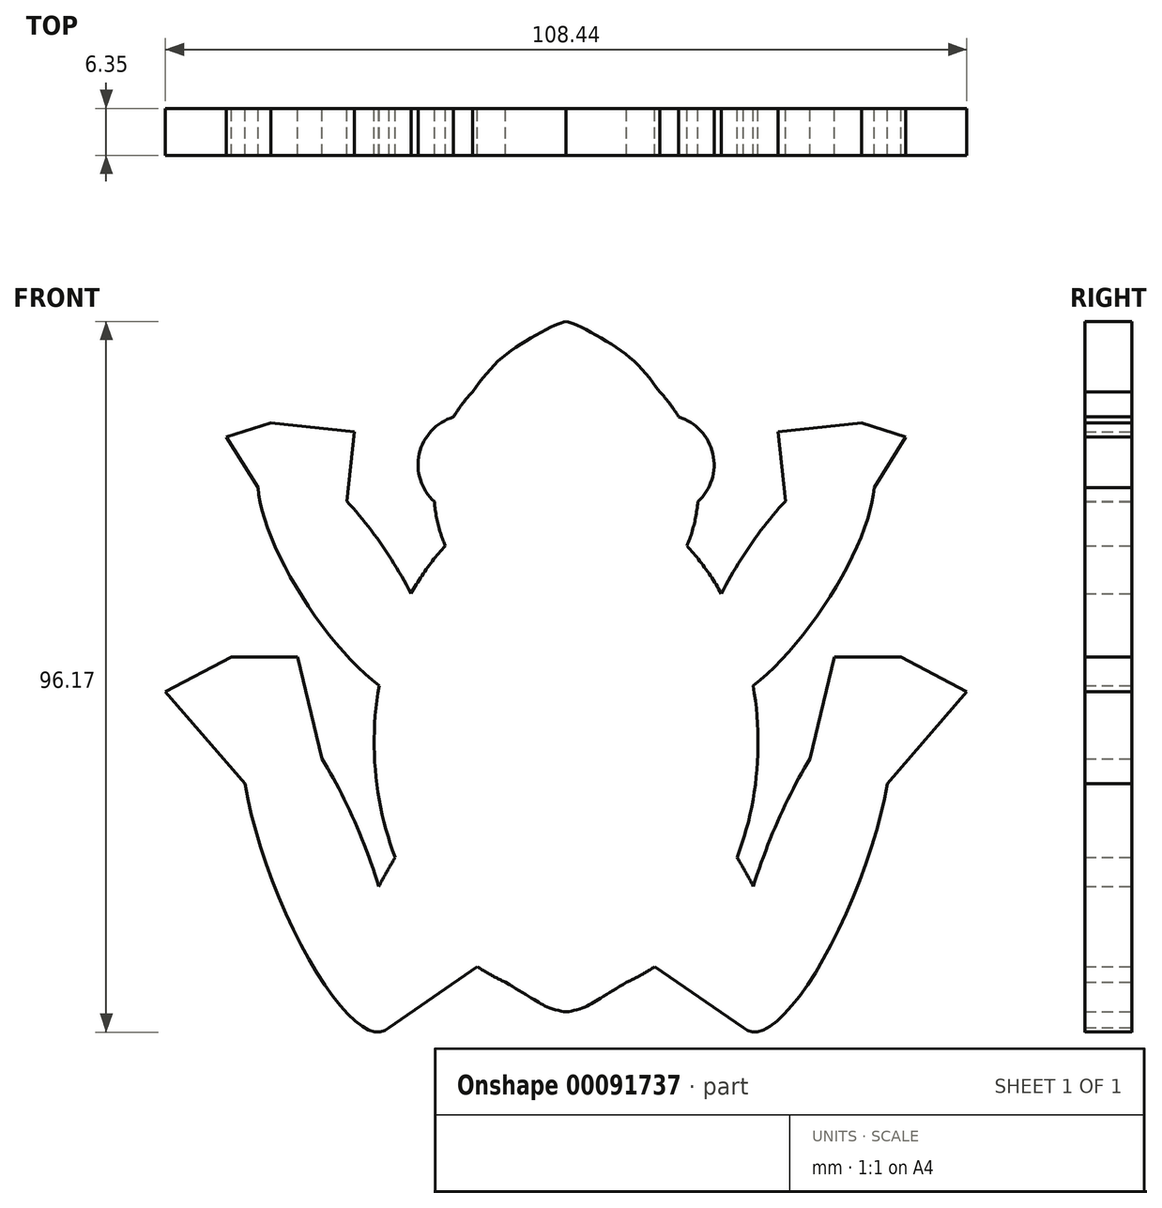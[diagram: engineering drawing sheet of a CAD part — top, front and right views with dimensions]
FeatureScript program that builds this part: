
annotation { "Feature Type Name" : "Feature", "Feature Type Description" : "" }
export const myFeature = defineFeature(function(context is Context, id is Id, definition is map)
    precondition{}
    {
        {
            var Q0;
            Q0=qCreatedBy(makeId("Front.planeOp"),FACE);
            var sketch = newSketch(context, id + "F0", { "sketchPlane" : qUnion([Q0])});
            skLineSegment(sketch, "E0", {"start": v(0, 61.38) * mm, "end": v(0, -64.6) * mm, "construction": true});
            skEllipticalArc(sketch, "E1", {});
            skEllipticalArc(sketch, "E2", {});
            skEllipticalArc(sketch, "E3", {});
            skEllipticalArc(sketch, "E4.trimOffspring", {});
            skEllipticalArc(sketch, "E5.trimOffspring", {});
            skEllipticalArc(sketch, "E6.trimOffspring", {});
            skEllipticalArc(sketch, "E7.trimOffspring", {});
            skArc(sketch, "E8", {"start": v(-15.23, 44.04) * mm, "mid": v(-19.86, 39.05) * mm, "end": v(-17.82, 32.57) * mm});
            skFitSpline(sketch, "E9", {"points": [v(-12.67, 47.44) * mm, v(-9.33, 51.47) * mm, v(-5.1, 54.5) * mm, v(-1.15, 56.62) * mm, v(0, 56.95) * mm], "startDerivative": vector(10.66, 14.6) * mm, "endDerivative": vector(7.04, 1.42) * mm});
            skEllipticalArc(sketch, "E10.trimOffspring", {});
            skFitSpline(sketch, "E11", {"points": [v(-8.18, -32.47) * mm, v(-4.1, -34.97) * mm, v(-2.03, -36) * mm, v(0, -36.45) * mm, v(0, -36.37) * mm], "startDerivative": vector(11.27, -6.95) * mm, "endDerivative": vector(-0.7, 1.73) * mm});
            skLineSegment(sketch, "E12", {"start": v(-41.7, 34.5) * mm, "end": v(-45.98, 41.36) * mm});
            skLineSegment(sketch, "E13", {"start": v(-45.98, 41.36) * mm, "end": v(-39.98, 43.24) * mm});
            skLineSegment(sketch, "E14", {"start": v(-39.98, 43.24) * mm, "end": v(-28.67, 42.02) * mm});
            skLineSegment(sketch, "E15", {"start": v(-28.67, 42.02) * mm, "end": v(-29.68, 32.66) * mm});
            skLineSegment(sketch, "E16", {"start": v(-43.48, -5.56) * mm, "end": v(-54.22, 6.86) * mm});
            skLineSegment(sketch, "E17", {"start": v(-54.22, 6.86) * mm, "end": v(-45.3, 11.53) * mm});
            skLineSegment(sketch, "E18", {"start": v(-45.3, 11.53) * mm, "end": v(-36.32, 11.53) * mm});
            skLineSegment(sketch, "E19", {"start": v(-36.32, 11.53) * mm, "end": v(-33, -2.25) * mm});
            skEllipticalArc(sketch, "E20.trimOffspring", {});
            skEllipticalArc(sketch, "E21.trimOffspring", {});
            skLineSegment(sketch, "E22.MirrorCS", {"start": v(45.98, 41.36) * mm, "end": v(39.98, 43.24) * mm});
            skLineSegment(sketch, "E23.MirrorCS", {"start": v(39.98, 43.24) * mm, "end": v(28.67, 42.02) * mm});
            skLineSegment(sketch, "E24.MirrorCS", {"start": v(28.67, 42.02) * mm, "end": v(29.68, 32.66) * mm});
            skLineSegment(sketch, "E25.MirrorCS", {"start": v(41.7, 34.5) * mm, "end": v(45.98, 41.36) * mm});
            skEllipticalArc(sketch, "E26.MirrorCS", {});
            skEllipticalArc(sketch, "E27.MirrorCS", {});
            skEllipticalArc(sketch, "E28.MirrorCS", {});
            skEllipticalArc(sketch, "E29.MirrorCS", {});
            skArc(sketch, "E30.MirrorCS", {"start": v(15.23, 44.04) * mm, "mid": v(19.86, 39.05) * mm, "end": v(17.82, 32.57) * mm});
            skEllipticalArc(sketch, "E31.MirrorCS", {});
            skEllipticalArc(sketch, "E32.MirrorCS", {});
            skEllipticalArc(sketch, "E33.MirrorCS", {});
            skEllipticalArc(sketch, "E34.MirrorCS", {});
            skFitSpline(sketch, "E35.MirrorCS", {"points": [v(8.18, -32.47) * mm, v(4.1, -34.97) * mm, v(2.03, -36) * mm, v(0, -36.45) * mm, v(0, -36.37) * mm], "startDerivative": vector(-11.27, -6.95) * mm, "endDerivative": vector(0.7, 1.73) * mm});
            skEllipticalArc(sketch, "E36.MirrorCS", {});
            skLineSegment(sketch, "E37.MirrorCS", {"start": v(43.48, -5.56) * mm, "end": v(54.22, 6.86) * mm});
            skLineSegment(sketch, "E38.MirrorCS", {"start": v(54.22, 6.86) * mm, "end": v(45.3, 11.53) * mm});
            skLineSegment(sketch, "E39.MirrorCS", {"start": v(45.3, 11.53) * mm, "end": v(36.32, 11.53) * mm});
            skLineSegment(sketch, "E40.MirrorCS", {"start": v(36.32, 11.53) * mm, "end": v(33, -2.25) * mm});
            skEllipticalArc(sketch, "E41.MirrorCS", {});
            skFitSpline(sketch, "E42.MirrorCS", {"points": [v(12.67, 47.44) * mm, v(9.33, 51.47) * mm, v(5.1, 54.5) * mm, v(1.15, 56.62) * mm, v(0, 56.95) * mm], "startDerivative": vector(-10.66, 14.6) * mm, "endDerivative": vector(-7.04, 1.42) * mm});
            skPoint(sketch, "E43.orphan", {"position": v(25.34, -19.48) * mm});
            skLineSegment(sketch, "E44", {"start": v(-24.73, -39.1) * mm, "end": v(-12, -30.34) * mm});
            skLineSegment(sketch, "E45", {"start": v(12, -30.34) * mm, "end": v(24.73, -39.1) * mm});
            skPoint(sketch, "E46.orphan", {"position": v(-25.34, -19.48) * mm});
            const initialGuessF0  = {"E1": [0, 0, 0, -1, 0.03420967608690262, 0.025975169580475122, 3.822228753432546, 4.082740239255983], "E2": [-0.033377982676029205, -0.01669064722955227, 0.36023211294631263, -0.9328627041543869, 0.02401154906528612, 0.006673159649137646, 1.3397548340325003, 2.159937264578693], "E3": [-0.02960868924856186, 0.022123347967863083, 0.5521623674682166, -0.8337366010628863, 0.019683908031495074, 0.006440496024383572, 1.2392978389962757, 2.0356558473371567], "E4.trimOffspring": [0, 0, 0, -1, 0.03420967608690262, 0.025975169580475122, 4.485743262777228, 5.184658428038163], "E5.trimOffspring": [0, 0, 0, -1, 0.03420967608690262, 0.025975169580475122, 5.803123768603595, 5.962800458505065], "E6.trimOffspring": [-0.011866778135299683, -0.01557948999106884, -0.5834284518425313, -0.8121645409525259, 0.02812887375094422, 0.009418747617529833, 4.947710183342089, 5.115212939531045], "E7.trimOffspring": [0, 0.03420967608690262, 0, -1, 0.018739966675639153, 0.017893049889585136, 3.9283800877434545, 4.160256833275168], "E10.trimOffspring": [0, 0.03420967608690262, 0, -1, 0.018739966675639153, 0.017893049889585136, 4.800212878716782, 5.131304363018152], "E20.trimOffspring": [-0.02960868924856186, 0.022123347967863083, 0.5521623674682166, -0.8337366010628863, 0.019683908031495074, 0.006440496024383572, 3.669813523805628, 5.5336689022255285], "E21.trimOffspring": [-0.033377982676029205, -0.01669064722955227, 0.36023211294631263, -0.9328627041543869, 0.02401154906528612, 0.006673159649137646, 4.088783709585892, 0.13197686408884035], "E26.MirrorCS": [0.02960868924856186, 0.022123347967863083, -0.5521623674682166, -0.8337366010628863, 0.019683908031495074, 0.006440496024383572, 0.7495164049540575, 2.613371783373958], "E27.MirrorCS": [0.02960868924856186, 0.022123347967863083, -0.5521623674682166, -0.8337366010628863, 0.019683908031495074, 0.006440496024383572, 4.247529459842429, 5.043887468183311], "E28.MirrorCS": [0, 0, 0, -1, 0.03420967608690262, 0.025975169580475122, 2.200445067923603, 2.46095655374704], "E29.MirrorCS": [0, 0.03420967608690262, 0, -1, 0.018739966675639153, 0.017893049889585136, 1.1518809441614344, 1.482972428462804], "E31.MirrorCS": [0, 0, 0, -1, 0.03420967608690262, 0.025975169580475122, 1.0985268791414233, 1.7974420444023584], "E32.MirrorCS": [0.011866778135299683, -0.01557948999106884, 0.5834284518425313, -0.8121645409525259, 0.02812887375094422, 0.009418747617529833, 1.1679723676485416, 1.3354751238374973], "E33.MirrorCS": [0.033377982676029205, -0.01669064722955227, -0.36023211294631263, -0.9328627041543869, 0.02401154906528612, 0.006673159649137646, 4.123248042600894, 4.943430473147086], "E34.MirrorCS": [0, 0, 0, -1, 0.03420967608690262, 0.025975169580475122, 0.32038484867452155, 0.4800615385759909], "E36.MirrorCS": [0.033377982676029205, -0.01669064722955227, -0.36023211294631263, -0.9328627041543869, 0.02401154906528612, 0.006673159649137646, 6.151208443090748, 2.1944015975936946], "E41.MirrorCS": [0, 0.03420967608690262, 0, -1, 0.018739966675639153, 0.017893049889585136, 2.122928473904418, 2.3548052194361317]};
            skSetInitialGuess(sketch, initialGuessF0);
            skSolve(sketch);
        }
        {
            var Q0;
            Q0 = qSketchRegion(id + "F0", true);
            extrude(context, id + "F1", {"entities" : qUnion([Q0]), "depth" : 6.35 * mm});
        }
    });
